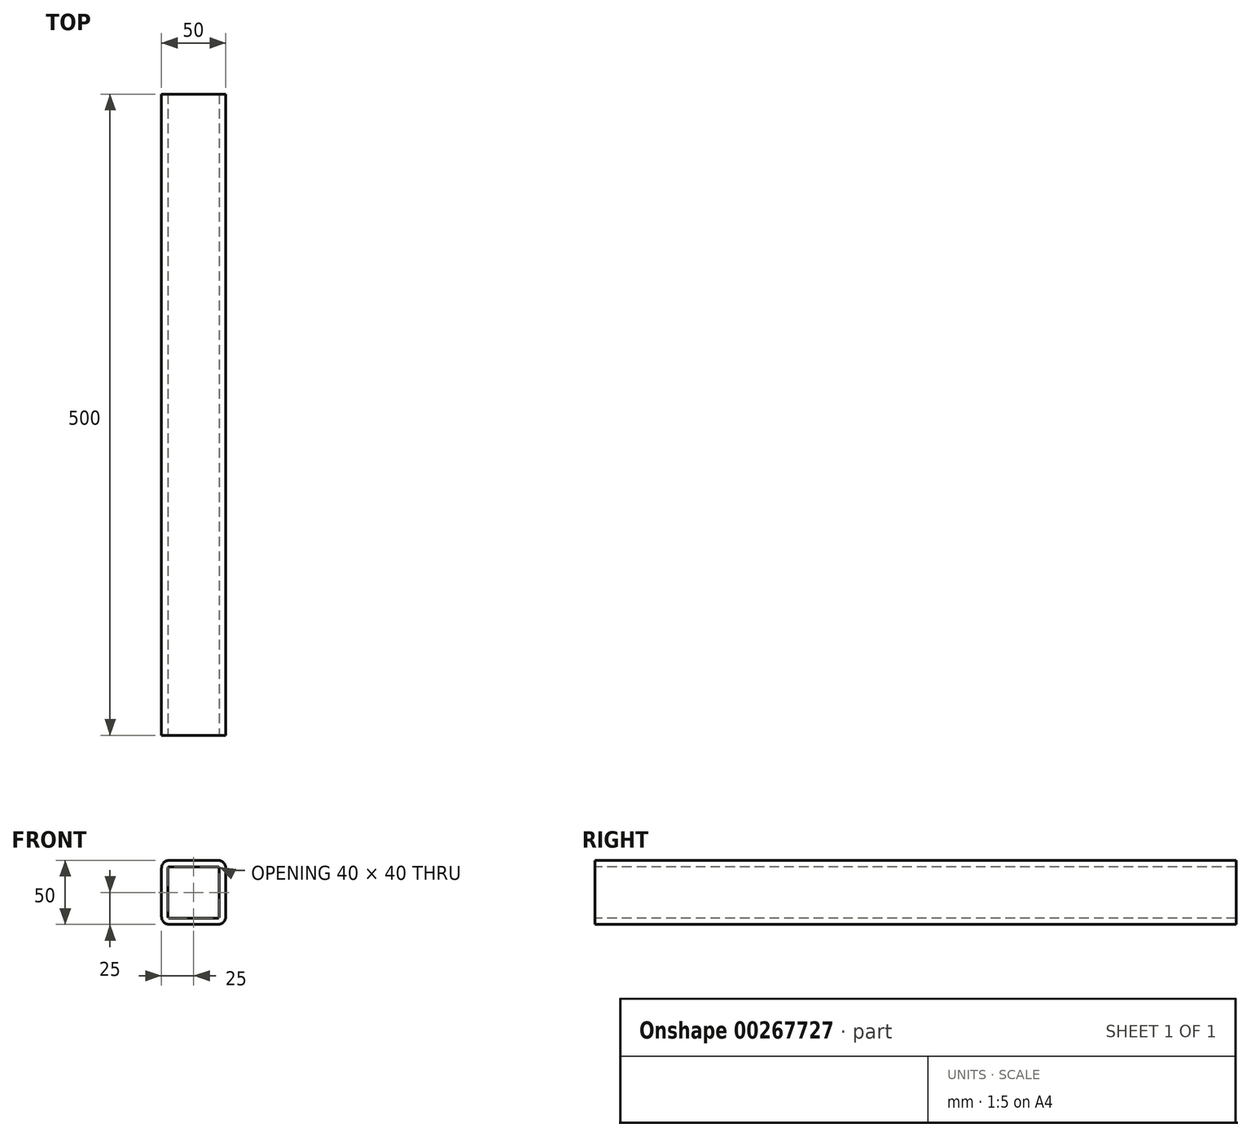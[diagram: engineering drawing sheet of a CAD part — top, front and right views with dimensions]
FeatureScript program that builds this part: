
annotation { "Feature Type Name" : "Feature", "Feature Type Description" : "" }
export const myFeature = defineFeature(function(context is Context, id is Id, definition is map)
    precondition{}
    {
        {
            var Q0;
            Q0=qCreatedBy(makeId("Front.planeOp"),FACE);
            var sketch = newSketch(context, id + "F0", { "sketchPlane" : qUnion([Q0])});
            skLineSegment(sketch, "E0.bottom", {"start": v(19, -25) * mm, "end": v(-19, -25) * mm});
            skLineSegment(sketch, "E0.top", {"start": v(19, 25) * mm, "end": v(-19, 25) * mm});
            skLineSegment(sketch, "E0.left", {"start": v(25, -19) * mm, "end": v(25, 19) * mm});
            skLineSegment(sketch, "E0.right", {"start": v(-25, -19) * mm, "end": v(-25, 19) * mm});
            skPoint(sketch, "E0.middle", {"position": v(0, 0) * mm});
            skPoint(sketch, "E1.visualSharp", {"position": v(-25, 25) * mm});
            skArc(sketch, "E1.filletArc", {"start": v(-19, 25) * mm, "mid": v(-23.24, 23.24) * mm, "end": v(-25, 19) * mm});
            skPoint(sketch, "E2.visualSharp", {"position": v(25, 25) * mm});
            skArc(sketch, "E2.filletArc", {"start": v(25, 19) * mm, "mid": v(23.24, 23.24) * mm, "end": v(19, 25) * mm});
            skPoint(sketch, "E3.visualSharp", {"position": v(25, -25) * mm});
            skArc(sketch, "E3.filletArc", {"start": v(19, -25) * mm, "mid": v(23.24, -23.24) * mm, "end": v(25, -19) * mm});
            skPoint(sketch, "E4.visualSharp", {"position": v(-25, -25) * mm});
            skArc(sketch, "E4.filletArc", {"start": v(-25, -19) * mm, "mid": v(-23.24, -23.24) * mm, "end": v(-19, -25) * mm});
            skArc(sketch, "E5.0", {"start": v(-20, -19) * mm, "mid": v(-19.7, -19.7) * mm, "end": v(-19, -20) * mm});
            skLineSegment(sketch, "E5.1", {"start": v(19, -20) * mm, "end": v(-19, -20) * mm});
            skLineSegment(sketch, "E5.2", {"start": v(-20, -19) * mm, "end": v(-20, 19) * mm});
            skArc(sketch, "E5.3", {"start": v(19, -20) * mm, "mid": v(19.7, -19.7) * mm, "end": v(20, -19) * mm});
            skArc(sketch, "E5.4", {"start": v(-19, 20) * mm, "mid": v(-19.7, 19.7) * mm, "end": v(-20, 19) * mm});
            skLineSegment(sketch, "E5.5", {"start": v(19, 20) * mm, "end": v(-19, 20) * mm});
            skArc(sketch, "E5.6", {"start": v(20, 19) * mm, "mid": v(19.7, 19.7) * mm, "end": v(19, 20) * mm});
            skLineSegment(sketch, "E5.7", {"start": v(20, -19) * mm, "end": v(20, 19) * mm});
            skSolve(sketch);
        }
        {
            var Q0;
            Q0=qSketchRegion(id+"F0",true);
            extrude(context, id + "F1", {"entities" : qUnion([Q0]), "oppositeDirection" : true, "depth" : 500 * mm});
        }
    });
